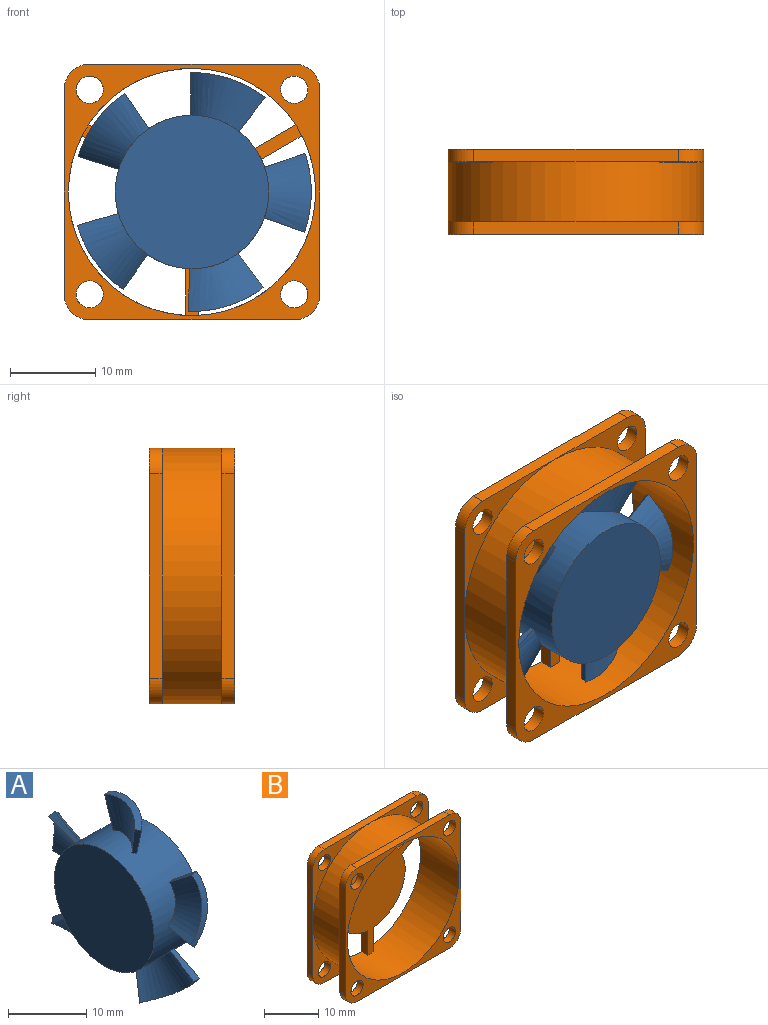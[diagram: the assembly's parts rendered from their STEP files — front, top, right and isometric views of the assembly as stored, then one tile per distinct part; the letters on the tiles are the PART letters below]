
ASSEMBLY  parts=2 mates=1
PART A: 28 faces, bbox 8.5x29.8x28.4 mm
  f0: cylinder r=14mm len=8.81mm, axis (1,0,0), area 9.8mm2, adj f22,f23,f24,f25
  f1: cylinder r=9mm len=18mm, axis (-1,0,0), area 460.5mm2, adj f2,f3,f4,f5,f6,f7,f8,f9
  f2: bspline ~8.51x4.96mm, area 35.5mm2, adj f1,f10,f11,f12
  f3: bspline ~9.79x5.53mm, area 43.5mm2, adj f1,f10,f11,f12
  f4: bspline ~9.65x9.06mm, area 43.3mm2, adj f1,f13,f14,f15
  f5: bspline ~9.33x8.89mm, area 36.8mm2, adj f1,f13,f14,f15
  f6: bspline ~9.31x7.67mm, area 43.3mm2, adj f1,f16,f17,f18
  f7: bspline ~8.65x7.87mm, area 36.8mm2, adj f1,f16,f17,f18
  f8: bspline ~9.86x9.63mm, area 43.3mm2, adj f1,f19,f20,f21
  f9: bspline ~8.41x8.18mm, area 36.8mm2, adj f1,f19,f20,f21
  f10: plane 4.76x1.78mm, normal (-0.16,0.93,-0.32), area 3.9mm2, adj f1,f2,f3,f11
  f11: cylinder r=14mm len=9.24mm, axis (1,0,0), area 9.8mm2, adj f2,f3,f10,f12
  f12: plane 4.94x2.04mm, normal (-0.73,-0.61,-0.32), area 3.9mm2, adj f1,f2,f3,f11
  f13: plane 4.92x2.14mm, normal (-0.73,0.68,-0.1), area 3.9mm2, adj f1,f4,f5,f14
  f14: cylinder r=14mm len=7.43mm, axis (1,0,0), area 9.8mm2, adj f4,f5,f13,f15
  f15: plane 4.19x2.94mm, normal (-0.16,-0.57,0.81), area 3.9mm2, adj f1,f4,f5,f14
  f16: plane 5.01x1.38mm, normal (-0.73,0.11,-0.68), area 3.9mm2, adj f1,f6,f7,f17
  f17: cylinder r=14mm len=8.76mm, axis (1,0,0), area 9.8mm2, adj f6,f7,f16,f18
  f18: plane 4.05x3.14mm, normal (-0.16,0.59,0.79), area 3.9mm2, adj f1,f6,f7,f17
  f19: plane 4.35x3.44mm, normal (-0.73,0.31,0.62), area 3.9mm2, adj f1,f8,f9,f20
  f20: cylinder r=14mm len=7.52mm, axis (1,0,0), area 9.8mm2, adj f8,f9,f19,f21
  f21: plane 4.83x1.55mm, normal (-0.16,-0.94,-0.29), area 3.9mm2, adj f1,f8,f9,f20
  f22: bspline ~8.5x8.14mm, area 39.2mm2, adj f0,f1,f23,f25
  f23: plane 5x1.07mm, normal (-0.16,-0.01,-0.99), area 3.9mm2, adj f0,f1,f22,f24
  f24: bspline ~9.31x7.7mm, area 43.3mm2, adj f0,f1,f23,f25
  f25: plane 4.41x3.36mm, normal (-0.73,-0.49,0.48), area 3.9mm2, adj f0,f1,f22,f24
  f26: plane 18x18mm, normal (1,0,0), area 254.5mm2, adj f1
  f27: plane 18x18mm, normal (-1,0,0), area 254.5mm2, adj f1
PART B: 46 faces, bbox 30x10x30 mm
  f0: cylinder r=1.6mm len=3.2mm, axis (0,1,0), area 15.1mm2, adj f11,f17
  f1: cylinder r=1.6mm len=3.2mm, axis (0,1,0), area 15.1mm2, adj f11,f19
  f2: cylinder r=1.6mm len=3.2mm, axis (0,1,0), area 15.1mm2, adj f11,f18
  f3: cylinder r=1.6mm len=3.2mm, axis (0,1,0), area 15.1mm2, adj f11,f16
  f4: cylinder r=1.6mm len=3.2mm, axis (0,-1,0), area 15.1mm2, adj f20,f24
  f5: cylinder r=1.6mm len=3.2mm, axis (0,-1,0), area 15.1mm2, adj f22,f24
  f6: cylinder r=1.6mm len=3.2mm, axis (0,-1,0), area 15.1mm2, adj f23,f24
  f7: cylinder r=1.6mm len=3.2mm, axis (0,-1,0), area 15.1mm2, adj f21,f24
  f8: cylinder r=9mm len=12.8mm, axis (0,-1,0), area 26mm2, adj f24,f25,f36,f37
  f9: cylinder r=15mm len=30mm, axis (0,-1,0), area 659.7mm2, adj f16,f17,f18,f19,f20,f21,f22,f23
  f10: cylinder r=14.5mm len=29mm, axis (0,1,0), area 904.3mm2, adj f11,f24,f25,f31,f32,f34,f35,f36
  f11: plane 30x30mm, normal (0,-1,0), area 199.6mm2, adj f0,f1,f2,f3,f10,f12,f13,f14
  f12: plane 24x1.5mm, normal (-1,0,0), area 36mm2, adj f11,f16,f17,f43,f45
  f13: plane 24x1.5mm, normal (0,0,1), area 36mm2, adj f11,f16,f19,f41,f43
  f14: plane 24x1.5mm, normal (1,0,0), area 36mm2, adj f11,f18,f19,f41,f44
  f15: plane 24x1.5mm, normal (0,0,-1), area 36mm2, adj f11,f17,f18,f44,f45
  f16: plane 15x15mm, normal (0,1,0), area 38.3mm2, adj f3,f9,f12,f13,f43
  f17: plane 15x15mm, normal (0,1,0), area 38.3mm2, adj f0,f9,f12,f15,f45
  f18: plane 15x15mm, normal (0,1,0), area 38.3mm2, adj f2,f9,f14,f15,f44
  f19: plane 15x15mm, normal (0,1,0), area 38.3mm2, adj f1,f9,f13,f14,f41
  f20: plane 15x15mm, normal (0,-1,0), area 38.3mm2, adj f4,f9,f26,f27,f42
  f21: plane 15x15mm, normal (0,-1,0), area 38.3mm2, adj f7,f9,f27,f28,f39
  f22: plane 15x15mm, normal (0,-1,0), area 38.3mm2, adj f5,f9,f28,f29,f40
  f23: plane 15x15mm, normal (0,-1,0), area 38.3mm2, adj f6,f9,f26,f29,f38
  f24: plane 30x30mm, normal (0,1,0), area 478.8mm2, adj f4,f5,f6,f7,f8,f10,f26,f27
  f25: plane 25.83x23.5mm, normal (0,-1,0), area 279.2mm2, adj f8,f10,f30,f31,f32,f33,f34,f35
  f26: plane 24x1.5mm, normal (0,0,-1), area 36mm2, adj f20,f23,f24,f38,f42
  f27: plane 24x1.5mm, normal (-1,0,0), area 36mm2, adj f20,f21,f24,f39,f42
  f28: plane 24x1.5mm, normal (0,0,1), area 36mm2, adj f21,f22,f24,f39,f40
  f29: plane 24x1.5mm, normal (1,0,0), area 36mm2, adj f22,f23,f24,f38,f40
  f30: cylinder r=9mm len=12.8mm, axis (0,-1,0), area 26mm2, adj f24,f25,f31,f32
  f31: plane 5.51x1.5mm, normal (-1,0,0), area 8.3mm2, adj f10,f24,f25,f30
  f32: plane 4.77x2.76mm, normal (-0.5,0,-0.87), area 8.3mm2, adj f10,f24,f25,f30
  f33: cylinder r=9mm len=14.78mm, axis (0,-1,0), area 26mm2, adj f24,f25,f34,f35
  f34: plane 4.77x2.76mm, normal (0.5,0,0.87), area 8.3mm2, adj f10,f24,f25,f33
  f35: plane 4.77x2.76mm, normal (-0.5,0,0.87), area 8.3mm2, adj f10,f24,f25,f33
  f36: plane 5.51x1.5mm, normal (1,0,0), area 8.3mm2, adj f8,f10,f24,f25
  f37: plane 4.77x2.76mm, normal (0.5,0,-0.87), area 8.3mm2, adj f8,f10,f24,f25
  f38: cylinder r=3mm len=3mm, axis (0,-1,0), area 7.1mm2, adj f23,f24,f26,f29
  f39: cylinder r=3mm len=3mm, axis (0,-1,0), area 7.1mm2, adj f21,f24,f27,f28
  f40: cylinder r=3mm len=3mm, axis (0,-1,0), area 7.1mm2, adj f22,f24,f28,f29
  f41: cylinder r=3mm len=3mm, axis (0,-1,0), area 7.1mm2, adj f11,f13,f14,f19
  f42: cylinder r=3mm len=3mm, axis (0,-1,0), area 7.1mm2, adj f20,f24,f26,f27
  f43: cylinder r=3mm len=3mm, axis (0,-1,0), area 7.1mm2, adj f11,f12,f13,f16
  f44: cylinder r=3mm len=3mm, axis (0,-1,0), area 7.1mm2, adj f11,f14,f15,f18
  f45: cylinder r=3mm len=3mm, axis (0,-1,0), area 7.1mm2, adj f11,f12,f15,f17
PLACE A rot(axis=(-0.58,0.58,-0.58),120deg) t=(-0.4,-35.45,15.94)mm
PLACE B t=(-0.4,-23.95,15.94)mm fixed
MATE revolute A.f0 <-> B.f8  axis (0,1,0) through (-0.4,-25.45,15.94)mm
